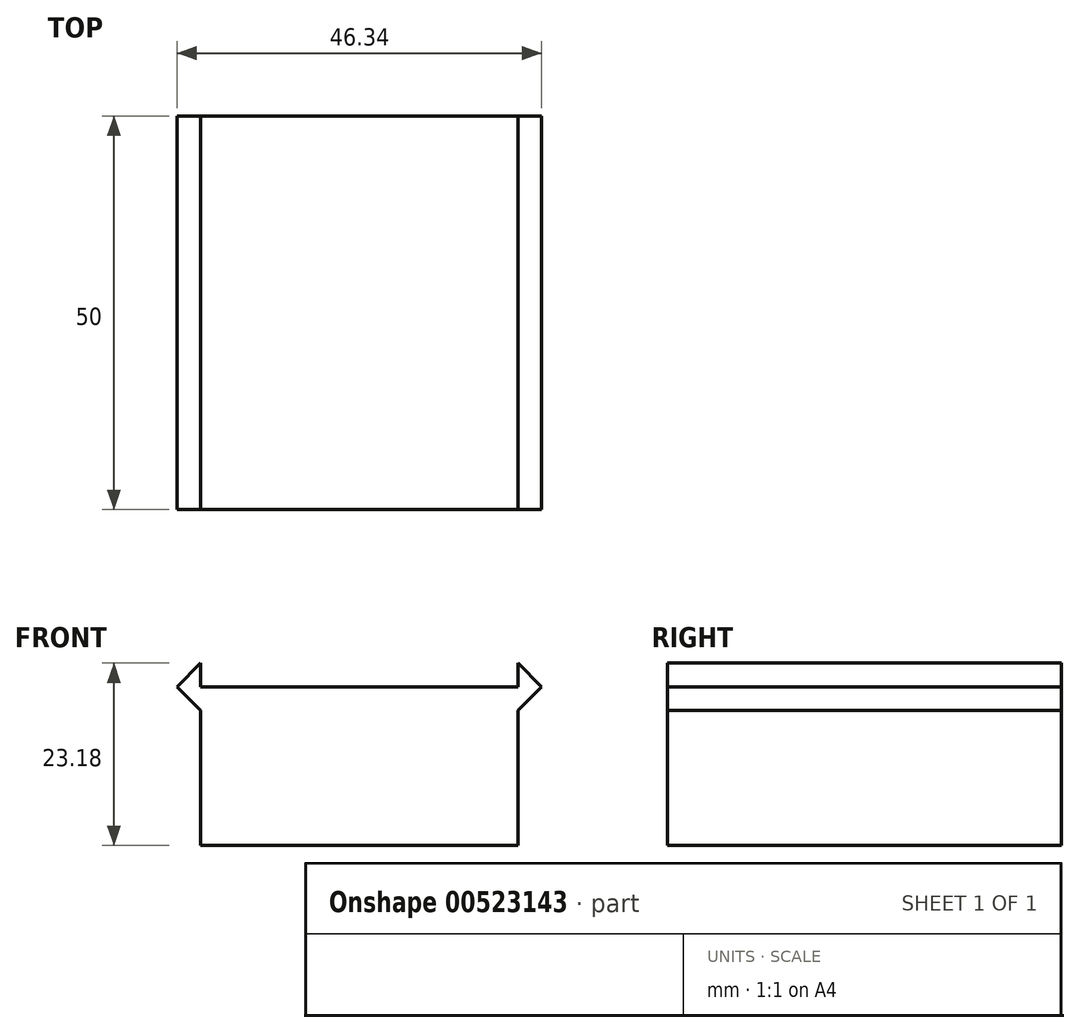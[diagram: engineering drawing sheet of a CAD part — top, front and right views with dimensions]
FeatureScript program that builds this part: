
annotation { "Feature Type Name" : "Feature", "Feature Type Description" : "" }
export const myFeature = defineFeature(function(context is Context, id is Id, definition is map)
    precondition{}
    {
        {
            var Q0;
            Q0=qCreatedBy(makeId("Front.planeOp"),FACE);
            var sketch = newSketch(context, id + "F0", { "sketchPlane" : qUnion([Q0])});
            skLineSegment(sketch, "E0", {"start": v(20.15, -10.07) * mm, "end": v(-20.15, -10.08) * mm});
            skLineSegment(sketch, "E1", {"start": v(-20.15, -10.08) * mm, "end": v(-20.15, 7.05) * mm});
            skLineSegment(sketch, "E2", {"start": v(-20.15, 7.05) * mm, "end": v(-23.17, 10.08) * mm});
            skLineSegment(sketch, "E3", {"start": v(-23.17, 10.08) * mm, "end": v(-20.15, 13.1) * mm});
            skLineSegment(sketch, "E4", {"start": v(-20.15, 13.1) * mm, "end": v(-20.15, 10.08) * mm});
            skLineSegment(sketch, "E5", {"start": v(-20.15, 10.08) * mm, "end": v(20.15, 10.08) * mm});
            skLineSegment(sketch, "E6", {"start": v(20.15, 10.08) * mm, "end": v(20.15, 13.1) * mm});
            skLineSegment(sketch, "E7", {"start": v(20.15, 13.1) * mm, "end": v(23.17, 10.08) * mm});
            skLineSegment(sketch, "E8", {"start": v(23.17, 10.08) * mm, "end": v(20.15, 7.05) * mm});
            skLineSegment(sketch, "E9", {"start": v(20.15, 7.05) * mm, "end": v(20.15, -10.07) * mm});
            skSolve(sketch);
        }
        {
            var Q0;
            Q0 = qSketchRegion(id + "F0", true);
            extrude(context, id + "F1", {"entities" : qUnion([Q0]), "endBound" : BoundingType.SYMMETRIC, "depth" : 50 * mm, "offsetDistance" : 25 * mm});
        }
    });
